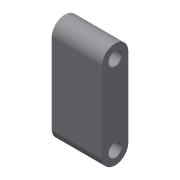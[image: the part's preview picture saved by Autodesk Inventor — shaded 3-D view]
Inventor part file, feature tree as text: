
AUTODESK INVENTOR PART (.ipt)
format: ipt  version: 2015 (Build 190159000, 159)  size: 81,920 bytes
history: native  units: mm
features: extrude x1, sketch x1
ambient origin geometry x8: Origin, YZ Plane, XZ Plane, XY Plane, X Axis, Y Axis, Z Axis, Center Point
bodies: Body1 (feature_tree)
feature tree (2):
  extrude  "Extrusion2"  Depth=0.5mm
  sketch  "Sketch2"  dims[d7=1.0mm d8=0.5mm d10=0.5mm d11=1.0mm d12=1.9mm d13=0.0mm]
